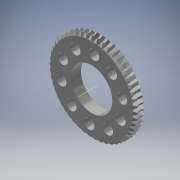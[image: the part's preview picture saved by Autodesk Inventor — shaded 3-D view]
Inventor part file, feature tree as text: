
AUTODESK INVENTOR PART (.ipt)
format: ipt  version: 2019.3 (Build 233278000, 278)  size: 1,051,648 bytes
history: native  units: mm (DEFAULTED — no unit token found)
features: other x8, plane x3, sketch x3, pattern_circular x2, extrude x1, hole x1
ambient origin geometry x5: Origin, X Axis, Y Axis, Z Axis, Center Point
bodies: Solid1 (feature_tree)
feature tree (18):
  other  "Tooth Plane"
  other  "Base Body Sketch"
  other  "Base Body"
  other  "Base Body2"
  plane  "Work Plane13"
  other  "Tooth"
  pattern_circular  "Tooth Pattern"  [2 undecoded]
  plane  "Work Plane14"
  plane  "Work Plane15"
  extrude  "Extrusion1"  Depth=6.35mm
  hole  "Hole3"  [1 undecoded]
  pattern_circular  "Circular Pattern2"  [2 undecoded]
  other  "Tooth Sketch"
  sketch  "Sketch8"  dims[d35=90.0deg]
  other  "Srf1"
  sketch  "Sketch9"  dims[d37=-1.23738mm]
  sketch  "Sketch10"  dims[d38=58.657497mm d39=3.490659mm d40=5.700281mm d41=8.125802mm d42=1.905mm d43=90.0deg d44=500.0mm d46=360.0deg d50=6.511309mm d68=58.657497mm d69=0.0mm d73=0.0mm d75=0.628319mm d77=101.063389mm d78=12.3mm d79=0.0mm d80=0.0mm d81=0.0mm d82=0.0mm d83=0.628319mm d84=0.0mm d85=180.0deg d86=58.657497mm d87=107.127192mm d89=12.209069mm d90=90.0deg d92=12.3mm d93=58.657497mm d94=50.546mm d95=25.4mm d96=0.0mm d97=38.1mm d98=12.7mm d99=19.05mm d100=7.0866mm d101=6.35mm d102=14.3117mm d103=25.4mm d104=20.594885mm d105=100.0mm d106=360.0deg]
  other  "Pitch Diameter"
note: 5 required parameter values undecoded (feature->parameter linkage not recoverable at this tier; creation-order binding heuristic only, values carry confidence <= 0.55)
